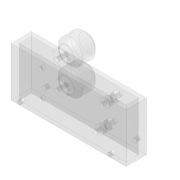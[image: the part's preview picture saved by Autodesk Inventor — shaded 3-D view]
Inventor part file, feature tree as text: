
AUTODESK INVENTOR PART (.ipt)
format: ipt  version: unknown  size: 293,376 bytes
history: native  units: in
note: dims shown in document units (in); Inventor stores cm internally (conversion verified against a paired STEP export)
features: extrude x8, sketch x8, projected_geometry x4, chamfer x1
ambient origin geometry x8: Origin, YZ Plane, XZ Plane, XY Plane, X Axis, Y Axis, Z Axis, Center Point
feature tree (21):
  extrude  "Extrusion40"  Depth=0.1181in
  extrude  "Extrusion41"  Depth=0.0787in
  extrude  "Extrusion42"  Depth=1.1811in
  extrude  "Extrusion43"  Depth=0.4724in
  extrude  "Extrusion44"  Depth=0.2756in
  extrude  "Extrusion45"  Depth=0.0787in TaperAngle=0.0deg
  chamfer  "Chamfer1"  Distance=0.2362in
  extrude  "Extrusion46"  Depth=0.1575in
  extrude  "Extrusion47"  Depth=0.1181in
  sketch  "Sketch41"  dims[d196=0.4724in d197=0.1181in]
  sketch  "Sketch42"  dims[d198=0.5118in d199=0.0787in]
  projected_geometry  "Projected Loop2"
  sketch  "Sketch43"  dims[d200=1.1811in d201=1.1811in]
  projected_geometry  "Projected Loop3"
  sketch  "Sketch44"  dims[d202=0.3937in d203=0.4724in]
  projected_geometry  "Projected Loop4"
  sketch  "Sketch45"  dims[d204=0.1575in d205=0.2756in]
  sketch  "Sketch46"  dims[d206=0.3937in d207=0.0in d208=0.0787in d209=0.0in]
  sketch  "Sketch47"  dims[d210=0.1575in d211=0.2362in d212=0.0in]
  sketch  "Sketch48"  dims[d213=0.0787in d214=0.1575in d215=0.1181in d216=0.1575in d217=0.5512in d218=0.0in d219=0.2756in d220=0.1181in d221=0.0in d222=0.4724in d223=0.4724in d224=0.3937in d225=0.0in d226=0.0787in d227=0.0787in d228=45.0deg d229=0.315in d230=0.0in d231=0.0787in d232=0.0787in d233=0.3937in d234=0.0in]
  projected_geometry  "Projected Loop5"
